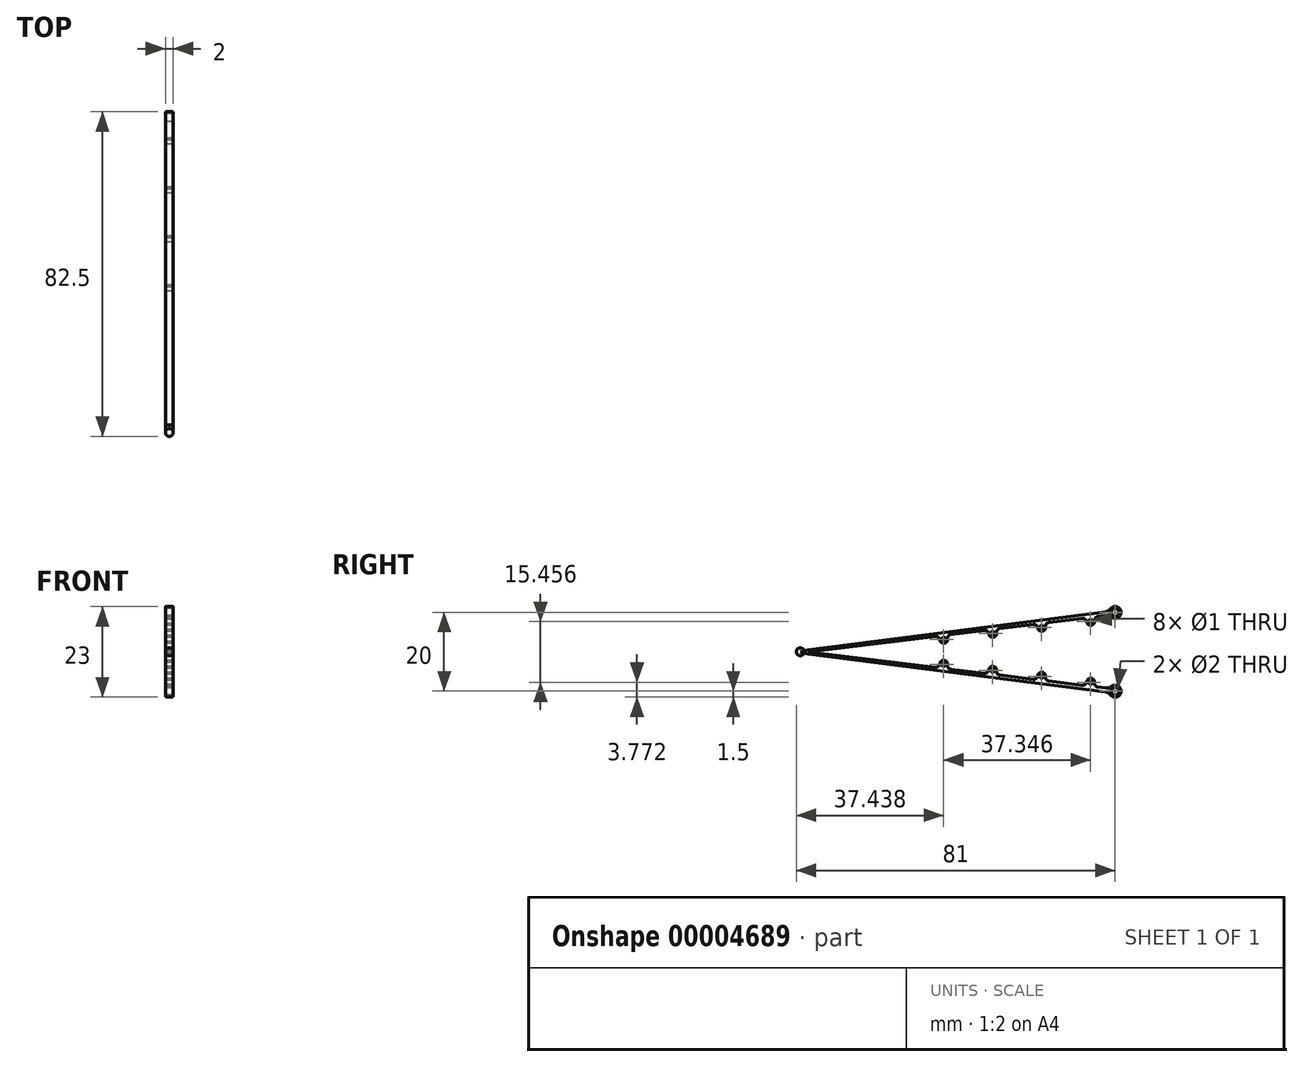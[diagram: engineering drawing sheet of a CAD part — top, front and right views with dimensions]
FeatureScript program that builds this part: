
annotation { "Feature Type Name" : "Feature", "Feature Type Description" : "" }
export const myFeature = defineFeature(function(context is Context, id is Id, definition is map)
    precondition{}
    {
        {
            var Q0;
            Q0=qCreatedBy(makeId("Right.planeOp"),FACE);
            var sketch = newSketch(context, id + "F0", { "sketchPlane" : qUnion([Q0])});
            skLineSegment(sketch, "E0", {"start": v(0, 0) * mm, "end": v(-80, 0) * mm, "construction": true});
            skLineSegment(sketch, "E1", {"start": v(0, 0) * mm, "end": v(0, 10) * mm, "construction": true});
            skArc(sketch, "E2", {"start": v(-0.91, 8.8) * mm, "mid": v(1.49, 10.19) * mm, "end": v(-1.18, 10.93) * mm});
            skCircle(sketch, "E3", {"center": v(0, 10) * mm, "radius": 1 * mm});
            skLineSegment(sketch, "E4", {"start": v(-77.98, 0) * mm, "end": v(-45.67, 3.93) * mm});
            skLineSegment(sketch, "E5", {"start": v(0, 10) * mm, "end": v(-80, 0) * mm, "construction": true});
            skLineSegment(sketch, "E6", {"start": v(-1.4, 9.82) * mm, "end": v(-1.47, 10.32) * mm, "construction": true});
            skLineSegment(sketch, "E7", {"start": v(-1.4, 9.82) * mm, "end": v(-1.34, 9.33) * mm, "construction": true});
            skLineSegment(sketch, "E8", {"start": v(-78.05, 0.5) * mm, "end": v(-2.49, 10.19) * mm});
            skLineSegment(sketch, "E9", {"start": v(-78.05, 0.5) * mm, "end": v(-77.98, 0) * mm, "construction": true});
            skPoint(sketch, "E10.visualSharp", {"position": v(-1.47, 10.32) * mm});
            skArc(sketch, "E10.filletArc", {"start": v(-2.49, 10.19) * mm, "mid": v(-1.76, 10.43) * mm, "end": v(-1.18, 10.93) * mm});
            skPoint(sketch, "E11.visualSharp", {"position": v(-1.34, 9.33) * mm});
            skArc(sketch, "E11.filletArc", {"start": v(-0.91, 8.8) * mm, "mid": v(-1.6, 9.15) * mm, "end": v(-2.37, 9.2) * mm});
            skLineSegment(sketch, "E12", {"start": v(-5.22, 7.85) * mm, "end": v(-5.22, 7.85) * mm});
            skLineSegment(sketch, "E13", {"start": v(-6.1, 6.74) * mm, "end": v(-6.1, 6.74) * mm});
            skLineSegment(sketch, "E14", {"start": v(-7.2, 7.6) * mm, "end": v(-7.2, 7.6) * mm});
            skLineSegment(sketch, "E15", {"start": v(-17.67, 6.33) * mm, "end": v(-17.67, 6.33) * mm});
            skLineSegment(sketch, "E16", {"start": v(-18.54, 5.22) * mm, "end": v(-18.54, 5.22) * mm});
            skLineSegment(sketch, "E17", {"start": v(-19.66, 6.1) * mm, "end": v(-19.66, 6.1) * mm});
            skLineSegment(sketch, "E18", {"start": v(-30.12, 4.82) * mm, "end": v(-30.12, 4.82) * mm});
            skLineSegment(sketch, "E19", {"start": v(-31, 3.7) * mm, "end": v(-31, 3.7) * mm});
            skLineSegment(sketch, "E20", {"start": v(-32.1, 4.58) * mm, "end": v(-32.1, 4.58) * mm});
            skLineSegment(sketch, "E21", {"start": v(-42.57, 3.3) * mm, "end": v(-42.57, 3.3) * mm});
            skLineSegment(sketch, "E22", {"start": v(-43.44, 2.19) * mm, "end": v(-43.44, 2.19) * mm});
            skLineSegment(sketch, "E23", {"start": v(-44.55, 3.06) * mm, "end": v(-44.55, 3.06) * mm});
            skLineSegment(sketch, "E24", {"start": v(-42.57, 3.3) * mm, "end": v(-32.1, 4.58) * mm, "construction": true});
            skLineSegment(sketch, "E25", {"start": v(-30.12, 4.82) * mm, "end": v(-19.66, 6.1) * mm, "construction": true});
            skLineSegment(sketch, "E26", {"start": v(-17.67, 6.33) * mm, "end": v(-7.2, 7.6) * mm, "construction": true});
            skLineSegment(sketch, "E27.trimOffspring", {"start": v(-4.35, 8.96) * mm, "end": v(-2.37, 9.2) * mm});
            skLineSegment(sketch, "E28.trimOffspring", {"start": v(-16.8, 7.45) * mm, "end": v(-8.32, 8.48) * mm});
            skLineSegment(sketch, "E29.trimOffspring", {"start": v(-29.25, 5.93) * mm, "end": v(-20.77, 6.96) * mm});
            skLineSegment(sketch, "E30.trimOffspring", {"start": v(-41.7, 4.42) * mm, "end": v(-33.22, 5.45) * mm});
            skPoint(sketch, "E31.visualSharp", {"position": v(-5.34, 8.84) * mm});
            skArc(sketch, "E31.filletArc", {"start": v(-4.35, 8.96) * mm, "mid": v(-5.02, 8.59) * mm, "end": v(-5.22, 7.85) * mm});
            skPoint(sketch, "E32.visualSharp", {"position": v(-5.1, 6.86) * mm});
            skArc(sketch, "E32.filletArc", {"start": v(-6.1, 6.74) * mm, "mid": v(-5.43, 7.11) * mm, "end": v(-5.22, 7.85) * mm});
            skPoint(sketch, "E33.visualSharp", {"position": v(-7.09, 6.61) * mm});
            skArc(sketch, "E33.filletArc", {"start": v(-7.2, 7.6) * mm, "mid": v(-6.83, 6.94) * mm, "end": v(-6.1, 6.74) * mm});
            skPoint(sketch, "E34.visualSharp", {"position": v(-7.33, 8.6) * mm});
            skArc(sketch, "E34.filletArc", {"start": v(-7.2, 7.6) * mm, "mid": v(-7.58, 8.27) * mm, "end": v(-8.32, 8.48) * mm});
            skPoint(sketch, "E35.visualSharp", {"position": v(-17.8, 7.33) * mm});
            skArc(sketch, "E35.filletArc", {"start": v(-16.8, 7.45) * mm, "mid": v(-17.47, 7.07) * mm, "end": v(-17.67, 6.33) * mm});
            skPoint(sketch, "E36.visualSharp", {"position": v(-17.55, 5.34) * mm});
            skArc(sketch, "E36.filletArc", {"start": v(-18.54, 5.22) * mm, "mid": v(-17.88, 5.6) * mm, "end": v(-17.67, 6.33) * mm});
            skPoint(sketch, "E37.visualSharp", {"position": v(-19.54, 5.1) * mm});
            skArc(sketch, "E37.filletArc", {"start": v(-19.66, 6.1) * mm, "mid": v(-19.28, 5.43) * mm, "end": v(-18.54, 5.22) * mm});
            skPoint(sketch, "E38.visualSharp", {"position": v(-19.78, 7.08) * mm});
            skArc(sketch, "E38.filletArc", {"start": v(-19.66, 6.1) * mm, "mid": v(-20.03, 6.76) * mm, "end": v(-20.77, 6.96) * mm});
            skPoint(sketch, "E39.visualSharp", {"position": v(-30.24, 5.81) * mm});
            skArc(sketch, "E39.filletArc", {"start": v(-29.25, 5.93) * mm, "mid": v(-29.92, 5.56) * mm, "end": v(-30.12, 4.82) * mm});
            skPoint(sketch, "E40.visualSharp", {"position": v(-30, 3.83) * mm});
            skArc(sketch, "E40.filletArc", {"start": v(-31, 3.7) * mm, "mid": v(-30.33, 4.08) * mm, "end": v(-30.12, 4.82) * mm});
            skPoint(sketch, "E41.visualSharp", {"position": v(-31.99, 3.58) * mm});
            skArc(sketch, "E41.filletArc", {"start": v(-32.1, 4.58) * mm, "mid": v(-31.73, 3.91) * mm, "end": v(-31, 3.7) * mm});
            skPoint(sketch, "E42.visualSharp", {"position": v(-32.23, 5.57) * mm});
            skArc(sketch, "E42.filletArc", {"start": v(-32.1, 4.58) * mm, "mid": v(-32.48, 5.24) * mm, "end": v(-33.22, 5.45) * mm});
            skPoint(sketch, "E43.visualSharp", {"position": v(-42.7, 4.3) * mm});
            skArc(sketch, "E43.filletArc", {"start": v(-41.7, 4.42) * mm, "mid": v(-42.36, 4.04) * mm, "end": v(-42.57, 3.3) * mm});
            skPoint(sketch, "E44.visualSharp", {"position": v(-42.45, 2.31) * mm});
            skArc(sketch, "E44.filletArc", {"start": v(-43.44, 2.19) * mm, "mid": v(-42.77, 2.57) * mm, "end": v(-42.57, 3.3) * mm});
            skPoint(sketch, "E45.visualSharp", {"position": v(-44.43, 2.07) * mm});
            skArc(sketch, "E45.filletArc", {"start": v(-44.55, 3.06) * mm, "mid": v(-44.18, 2.4) * mm, "end": v(-43.44, 2.19) * mm});
            skPoint(sketch, "E46.visualSharp", {"position": v(-44.68, 4.05) * mm});
            skArc(sketch, "E46.filletArc", {"start": v(-44.55, 3.06) * mm, "mid": v(-44.93, 3.73) * mm, "end": v(-45.67, 3.93) * mm});
            skLineSegment(sketch, "E47", {"start": v(-17.67, 6.33) * mm, "end": v(-19.66, 6.1) * mm, "construction": true});
            skLineSegment(sketch, "E48", {"start": v(-30.12, 4.82) * mm, "end": v(-32.1, 4.58) * mm, "construction": true});
            skLineSegment(sketch, "E49", {"start": v(-42.57, 3.3) * mm, "end": v(-44.55, 3.06) * mm, "construction": true});
            skLineSegment(sketch, "E50", {"start": v(-7.2, 7.6) * mm, "end": v(-5.22, 7.85) * mm, "construction": true});
            skCircle(sketch, "E51", {"center": v(-6.22, 7.73) * mm, "radius": 0.5 * mm});
            skCircle(sketch, "E52", {"center": v(-18.66, 6.21) * mm, "radius": 0.5 * mm});
            skCircle(sketch, "E53", {"center": v(-31.11, 4.7) * mm, "radius": 0.5 * mm});
            skCircle(sketch, "E54", {"center": v(-43.56, 3.18) * mm, "radius": 0.5 * mm});
            skLineSegment(sketch, "E55", {"start": v(-78.05, 0.5) * mm, "end": v(-80, 0) * mm});
            skLineSegment(sketch, "E56", {"start": v(-80, 0) * mm, "end": v(-77.98, 0) * mm});
            skPoint(sketch, "E57", {"position": v(-78.02, 0.25) * mm});
            skSolve(sketch);
        }
        {
            var Q0;
            Q0 = qSketchRegion(id + "F0", true);
            extrude(context, id + "F1", {"entities" : qUnion([Q0]), "depth" : 2 * mm});
        }
        {
            var Q0;
            Q0=makeQuery(id+"F1.opExtrude","SWEPT_BODY",BODY,{"disambiguationData":[OSD([sQuery(id+"F0.wireOp",EDGE,"E2"),sQuery(id+"F0.wireOp",EDGE,"E3"),sQuery(id+"F0.wireOp",EDGE,"39fec1f6-cf8f-4d41-aa4d-b3a44edeef19"),sQuery(id+"F0.wireOp",EDGE,"E4"),sQuery(id+"F0.wireOp",EDGE,"8078b3fb-b842-4e34-b5e9-cf22721ff5a8.filletArc"),sQuery(id+"F0.wireOp",EDGE,"0f908dc7-c1f3-4107-a7d9-337319445088.filletArc"),sQuery(id+"F0.wireOp",EDGE,"E8"),sQuery(id+"F0.wireOp",EDGE,"E10.filletArc"),sQuery(id+"F0.wireOp",EDGE,"E11.filletArc"),sQuery(id+"F0.wireOp",EDGE,"E27.trimOffspring"),sQuery(id+"F0.wireOp",EDGE,"E28.trimOffspring"),sQuery(id+"F0.wireOp",EDGE,"E29.trimOffspring"),sQuery(id+"F0.wireOp",EDGE,"E30.trimOffspring"),sQuery(id+"F0.wireOp",EDGE,"E31.filletArc"),sQuery(id+"F0.wireOp",EDGE,"E32.filletArc"),sQuery(id+"F0.wireOp",EDGE,"E33.filletArc"),sQuery(id+"F0.wireOp",EDGE,"E34.filletArc"),sQuery(id+"F0.wireOp",EDGE,"E35.filletArc"),sQuery(id+"F0.wireOp",EDGE,"E36.filletArc"),sQuery(id+"F0.wireOp",EDGE,"E37.filletArc"),sQuery(id+"F0.wireOp",EDGE,"E38.filletArc"),sQuery(id+"F0.wireOp",EDGE,"E39.filletArc"),sQuery(id+"F0.wireOp",EDGE,"E40.filletArc"),sQuery(id+"F0.wireOp",EDGE,"E41.filletArc"),sQuery(id+"F0.wireOp",EDGE,"E42.filletArc"),sQuery(id+"F0.wireOp",EDGE,"E43.filletArc"),sQuery(id+"F0.wireOp",EDGE,"E44.filletArc"),sQuery(id+"F0.wireOp",EDGE,"E45.filletArc"),sQuery(id+"F0.wireOp",EDGE,"E46.filletArc"),sQuery(id+"F0.wireOp",EDGE,"E51"),sQuery(id+"F0.wireOp",EDGE,"E52"),sQuery(id+"F0.wireOp",EDGE,"E53"),sQuery(id+"F0.wireOp",EDGE,"E54")])]});
            var Q1;
            Q1=qCreatedBy(makeId("Top.planeOp"),FACE);
            mirror(context, id + "F2", {"entities" : qUnion([Q0]), "mirrorPlane" : qUnion([Q1])});
        }
        {
            var Q0;
            Q0=makeQuery(id+"F1.opExtrude","SWEPT_BODY",BODY,{"disambiguationData":[OSD([sQuery(id+"F0.wireOp",EDGE,"E2"),sQuery(id+"F0.wireOp",EDGE,"E3"),sQuery(id+"F0.wireOp",EDGE,"39fec1f6-cf8f-4d41-aa4d-b3a44edeef19"),sQuery(id+"F0.wireOp",EDGE,"E4"),sQuery(id+"F0.wireOp",EDGE,"8078b3fb-b842-4e34-b5e9-cf22721ff5a8.filletArc"),sQuery(id+"F0.wireOp",EDGE,"0f908dc7-c1f3-4107-a7d9-337319445088.filletArc"),sQuery(id+"F0.wireOp",EDGE,"E8"),sQuery(id+"F0.wireOp",EDGE,"E10.filletArc"),sQuery(id+"F0.wireOp",EDGE,"E11.filletArc"),sQuery(id+"F0.wireOp",EDGE,"E27.trimOffspring"),sQuery(id+"F0.wireOp",EDGE,"E28.trimOffspring"),sQuery(id+"F0.wireOp",EDGE,"E29.trimOffspring"),sQuery(id+"F0.wireOp",EDGE,"E30.trimOffspring"),sQuery(id+"F0.wireOp",EDGE,"E31.filletArc"),sQuery(id+"F0.wireOp",EDGE,"E32.filletArc"),sQuery(id+"F0.wireOp",EDGE,"E33.filletArc"),sQuery(id+"F0.wireOp",EDGE,"E34.filletArc"),sQuery(id+"F0.wireOp",EDGE,"E35.filletArc"),sQuery(id+"F0.wireOp",EDGE,"E36.filletArc"),sQuery(id+"F0.wireOp",EDGE,"E37.filletArc"),sQuery(id+"F0.wireOp",EDGE,"E38.filletArc"),sQuery(id+"F0.wireOp",EDGE,"E39.filletArc"),sQuery(id+"F0.wireOp",EDGE,"E40.filletArc"),sQuery(id+"F0.wireOp",EDGE,"E41.filletArc"),sQuery(id+"F0.wireOp",EDGE,"E42.filletArc"),sQuery(id+"F0.wireOp",EDGE,"E43.filletArc"),sQuery(id+"F0.wireOp",EDGE,"E44.filletArc"),sQuery(id+"F0.wireOp",EDGE,"E45.filletArc"),sQuery(id+"F0.wireOp",EDGE,"E46.filletArc"),sQuery(id+"F0.wireOp",EDGE,"E51"),sQuery(id+"F0.wireOp",EDGE,"E52"),sQuery(id+"F0.wireOp",EDGE,"E53"),sQuery(id+"F0.wireOp",EDGE,"E54")])]});
            var Q1;
            Q1=makeQuery(id+"F2.opPattern","COPY",BODY,{"derivedFrom":makeQuery(id+"F1.opExtrude","SWEPT_BODY",BODY,{"disambiguationData":[OSD([sQuery(id+"F0.wireOp",EDGE,"E2"),sQuery(id+"F0.wireOp",EDGE,"E3"),sQuery(id+"F0.wireOp",EDGE,"39fec1f6-cf8f-4d41-aa4d-b3a44edeef19"),sQuery(id+"F0.wireOp",EDGE,"E4"),sQuery(id+"F0.wireOp",EDGE,"8078b3fb-b842-4e34-b5e9-cf22721ff5a8.filletArc"),sQuery(id+"F0.wireOp",EDGE,"0f908dc7-c1f3-4107-a7d9-337319445088.filletArc"),sQuery(id+"F0.wireOp",EDGE,"E8"),sQuery(id+"F0.wireOp",EDGE,"E10.filletArc"),sQuery(id+"F0.wireOp",EDGE,"E11.filletArc"),sQuery(id+"F0.wireOp",EDGE,"E27.trimOffspring"),sQuery(id+"F0.wireOp",EDGE,"E28.trimOffspring"),sQuery(id+"F0.wireOp",EDGE,"E29.trimOffspring"),sQuery(id+"F0.wireOp",EDGE,"E30.trimOffspring"),sQuery(id+"F0.wireOp",EDGE,"E31.filletArc"),sQuery(id+"F0.wireOp",EDGE,"E32.filletArc"),sQuery(id+"F0.wireOp",EDGE,"E33.filletArc"),sQuery(id+"F0.wireOp",EDGE,"E34.filletArc"),sQuery(id+"F0.wireOp",EDGE,"E35.filletArc"),sQuery(id+"F0.wireOp",EDGE,"E36.filletArc"),sQuery(id+"F0.wireOp",EDGE,"E37.filletArc"),sQuery(id+"F0.wireOp",EDGE,"E38.filletArc"),sQuery(id+"F0.wireOp",EDGE,"E39.filletArc"),sQuery(id+"F0.wireOp",EDGE,"E40.filletArc"),sQuery(id+"F0.wireOp",EDGE,"E41.filletArc"),sQuery(id+"F0.wireOp",EDGE,"E42.filletArc"),sQuery(id+"F0.wireOp",EDGE,"E43.filletArc"),sQuery(id+"F0.wireOp",EDGE,"E44.filletArc"),sQuery(id+"F0.wireOp",EDGE,"E45.filletArc"),sQuery(id+"F0.wireOp",EDGE,"E46.filletArc"),sQuery(id+"F0.wireOp",EDGE,"E51"),sQuery(id+"F0.wireOp",EDGE,"E52"),sQuery(id+"F0.wireOp",EDGE,"E53"),sQuery(id+"F0.wireOp",EDGE,"E54")])]}),"instanceName":"1"});
            booleanBodies(context, id + "F3", {"operationType" : BooleanOperationType.UNION, "tools" : qUnion([Q0, Q1])});
        }
        {
            var Q0;
            Q0=qCreatedBy(makeId("Right.planeOp"),FACE);
            cPlane(context, id + "F4", {"entities" : qUnion([Q0]), "cplaneType" : CPlaneType.OFFSET, "offset" : 1 * mm, "width" : 150 * mm, "height" : 150 * mm});
        }
        {
            var Q0;
            Q0=qCreatedBy(id+"F4.planeOp",FACE);
            var sketch = newSketch(context, id + "F5", { "sketchPlane" : qUnion([Q0])});
            skArc(sketch, "E58", {"start": v(-79, 0) * mm, "mid": v(-80, 1) * mm, "end": v(-81, 0) * mm});
            skLineSegment(sketch, "E59", {"start": v(-79, 0) * mm, "end": v(-81, 0) * mm, "construction": true});
            skLineSegment(sketch, "E60", {"start": v(-81, 0) * mm, "end": v(-79, 0) * mm});
            skSolve(sketch);
        }
        {
            var Q0;
            Q0 = qSketchRegion(id + "F5", true);
            var Q1;
            Q1=sQuery(id+"F5.wireOp",EDGE,"E60");
            revolve(context, id + "F6", {"operationType" : NewBodyOperationType.ADD, "entities" : qUnion([Q0]), "axis" : qUnion([Q1]), "revolveType" : RevolveType.FULL});
        }
    });
